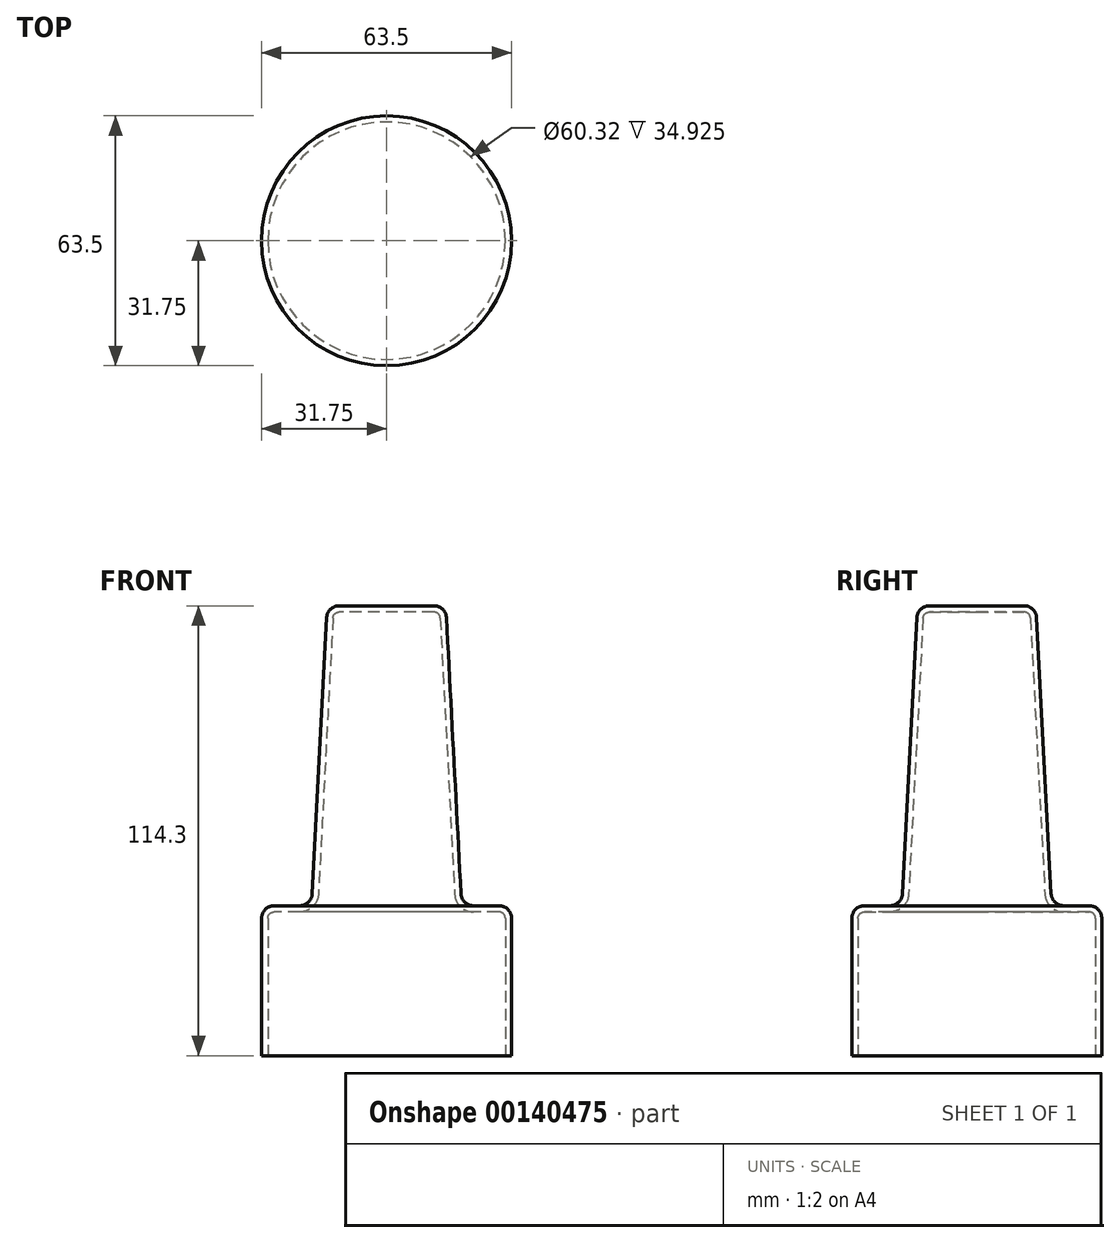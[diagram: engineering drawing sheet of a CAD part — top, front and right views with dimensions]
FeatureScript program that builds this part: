
annotation { "Feature Type Name" : "Feature", "Feature Type Description" : "" }
export const myFeature = defineFeature(function(context is Context, id is Id, definition is map)
    precondition{}
    {
        {
            var Q0;
            Q0=qCreatedBy(makeId("Top.planeOp"),FACE);
            var sketch = newSketch(context, id + "F3", { "sketchPlane" : qUnion([Q0])});
            skCircle(sketch, "E0", {"center": v(0, 0) * mm, "radius": 31.75 * mm});
            skSolve(sketch);
        }
        {
            var Q0;
            Q0 = qSketchRegion(id + "F3", true);
            extrude(context, id + "F0", {"entities" : qUnion([Q0]), "depth" : 38.1 * mm});
        }
        {
            var Q0;
            Q0=makeQuery(id+"F0.opExtrude","CAP_FACE",FACE,{"disambiguationData":[OSD([sQuery(id+"F3.wireOp",EDGE,"E0")])],"isStart":false});
            var sketch = newSketch(context, id + "F1", { "sketchPlane" : qUnion([Q0])});
            skCircle(sketch, "E1", {"center": v(0, 0) * mm, "radius": 19.05 * mm});
            skSolve(sketch);
        }
        {
            var Q0;
            Q0 = qSketchRegion(id + "F1", true);
            extrude(context, id + "F4", {"entities" : qUnion([Q0]), "operationType" : NewBodyOperationType.ADD, "depth" : 76.2 * mm, "hasDraft" : true, "draftAngle" : 3 * degree, "draftPullDirection" : true});
        }
        {
            var Q0;
            Q0=makeQuery(id+"F4.opExtrude","SWEPT_FACE",FACE,{"disambiguationData":[OSD([sQuery(id+"F1.wireOp",EDGE,"E1")])]});
            var Q1;
            Q1=makeQuery(id+"F0.opExtrude","CAP_EDGE",EDGE,{"disambiguationData":[OSD([sQuery(id+"F3.wireOp",EDGE,"E0")])],"isStart":false});
            fillet(context, id + "F2", {"entities" : qUnion([Q0, Q1]), "radius" : 3.17 * mm, "tangentPropagation" : true, "allowEdgeOverflow" : false});
        }
        {
            var Q0;
            Q0=makeQuery(id+"F0.opExtrude","CAP_FACE",FACE,{"disambiguationData":[OSD([sQuery(id+"F3.wireOp",EDGE,"E0")])],"isStart":true});
            shell(context, id + "F5", {"entities" : qUnion([Q0]), "thickness" : 1.59 * mm});
        }
    });
